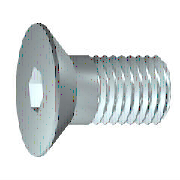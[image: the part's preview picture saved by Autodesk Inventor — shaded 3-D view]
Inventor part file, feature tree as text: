
AUTODESK INVENTOR PART (.ipt)
format: ipt  version: 2015 (Build 190159000, 159)  size: 183,296 bytes
history: native  units: mm (DEFAULTED — no unit token found)
features: sketch x2, extrude x1, plane x1
ambient origin geometry x7: Origin, YZ Plane, XY Plane, X Axis, Y Axis, Z Axis, Center Point
bodies: Solid1 (feature_tree), Body (feature_tree)
feature tree (4):
  sketch  "Sketch2"  dims[d2=1.3mm d3=3.0mm d6=1.86mm d7=45.0deg d8=2.309401mm d9=60.0deg d10=5.54mm d11=3.0mm d12=0.306725mm d13=90.0deg d30=10.0mm d14=0.0mm d15=4.0mm d16=0.0mm d17=0.306725mm d18=0.306725mm d20=0.0mm d39=45.0deg d43=0.0mm d44=0.0mm]
  extrude  "Slot"  Depth=4.0mm
  plane  "Work Plane1"
  sketch  "Sketch1"  dims[d0=8.0mm d1=4.0mm]
